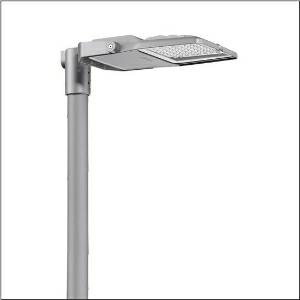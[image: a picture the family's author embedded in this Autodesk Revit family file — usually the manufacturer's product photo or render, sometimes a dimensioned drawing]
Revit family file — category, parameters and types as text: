
# Revit family: floodlight_fl_21_iq_mini___pl61_5xa7772d4c3a_23c5
name_source: partatom
category: Lighting Fixtures
units: mm (PartAtom-declared; Revit-internal decimal feet)

## family parameters
Cut with Voids When Loaded = No
Host = Face
Light Source = No
Part Type = Normal
Room Calculation Point = No
Round Connector Dimension = Use Diameter
Shared = No

## types (1)
- --- (1 x LED, 18260 lm, 143 W, 4000K)
    Apparent Load = 143 VA
    CIE Flux Codes = 33 65 98 100 100
    Color Rendering = 70
    Color Temperature = 4000K
    Default Elevation = 1800 mm
    Description = Floodlight FL 21 iQ mini, floodlight, primary light control with lens, of PMMA, primary optical cover: protective disc, of toughened safety glass, transparent, light distribution: PL61, light emission: direct distribution, installation type: surface-mounted, LED, High Power LED, rated luminous flux: 18.260lm, luminous efficacy: 128lm/W, light colour: 740, colour temperature: 4000K, control gear: iQ Street-Remote/DALI, control: Auto-Match, Temp-Guard, Night-Set, Smart-Wire, Desk-Remote (wireless, voltage-free reading and setting of iQ features in the workshop via application-optimized NFC function/RFID function), optimised constant luminous flux control (CLO 2.0), Light-Fading, Lumen-Switch, with terminal, 6-pole, mains connection: 220..240V, AC, 50/60Hz, start of lifetime: 143W, end of service life: 152W, reduction: 61W, luminaire housing, of diecast aluminium, powder-coated, Siteco® metallic grey (DB 702S), corrosivity category C5 mid according to DIN EN ISO 12944, suitable for swimming pools, chlorine-resistant, sealing non-destructively replaceable, please order mast flange separately, mast bracket, of steel, galvanised, powder-coated, protection rating (complete): IP66, insulation class (complete): insulation class II (safety insulation), certification: CE, ENEC, VDE, protection symbol: D, impact resistance: IK08, permissible operating ambient temperature: -40..+40°C, permissible operating ambient temperature for outdoor applications: -40..+50°C, standard: DIN EN 12944, LABS conformity tested according to VDMA 24364:2018-05, packaging unit: 1 piece

Light Distribution: PL61
    Height = 70 mm
    Lamp = 1 x LED
    Lamp Light Flux = 18260 lm
    Lamp Power = 143 W
    Lamp count = 1
    Length = 485 mm
    Luminous efficacy = 128 lm/W
    Manufacturer = Siteco
    ModVariant = No
    Model = 5XA7772D4C3A
    Number of Poles = 1
    OnlyDefault = Yes
    Power Factor = 1
    Product Name = Floodlight FL 21 iQ mini | PL61
    Product group = floodlight | pylon annexe
    ProductGroupID = 6200
    Protection Class = Protection class II
    Protection Degree = IP 66
    RLX_Detail_Level = 1
    RLX_Emergency_Light_Flux = 0 lm
    RLX_Emergency_Type = 0
    RLX_Emergency_Type_DB = No
    RlxData = <blob elided: 101725 chars, md5=7b89ed8d>
    Socket = socket
    Standby Power = 0 W
    System Light Flux = 18260 lm
    System Power = 143 W
    Type Comments = factory setting: luminous flux: 100 % | dim-lin: 254 | 730 mA
    Type Image = l_1007125.jpg
    URL = http://relux.com
    VarID = @adj_172300
    Voltage = 0 V
    Weight = 0.00 kg
    Width = 337 mm

## geometry (parser evidence)
native form markers: Blend x4, Sweep x11
no freeform markers — native parametric forms only
